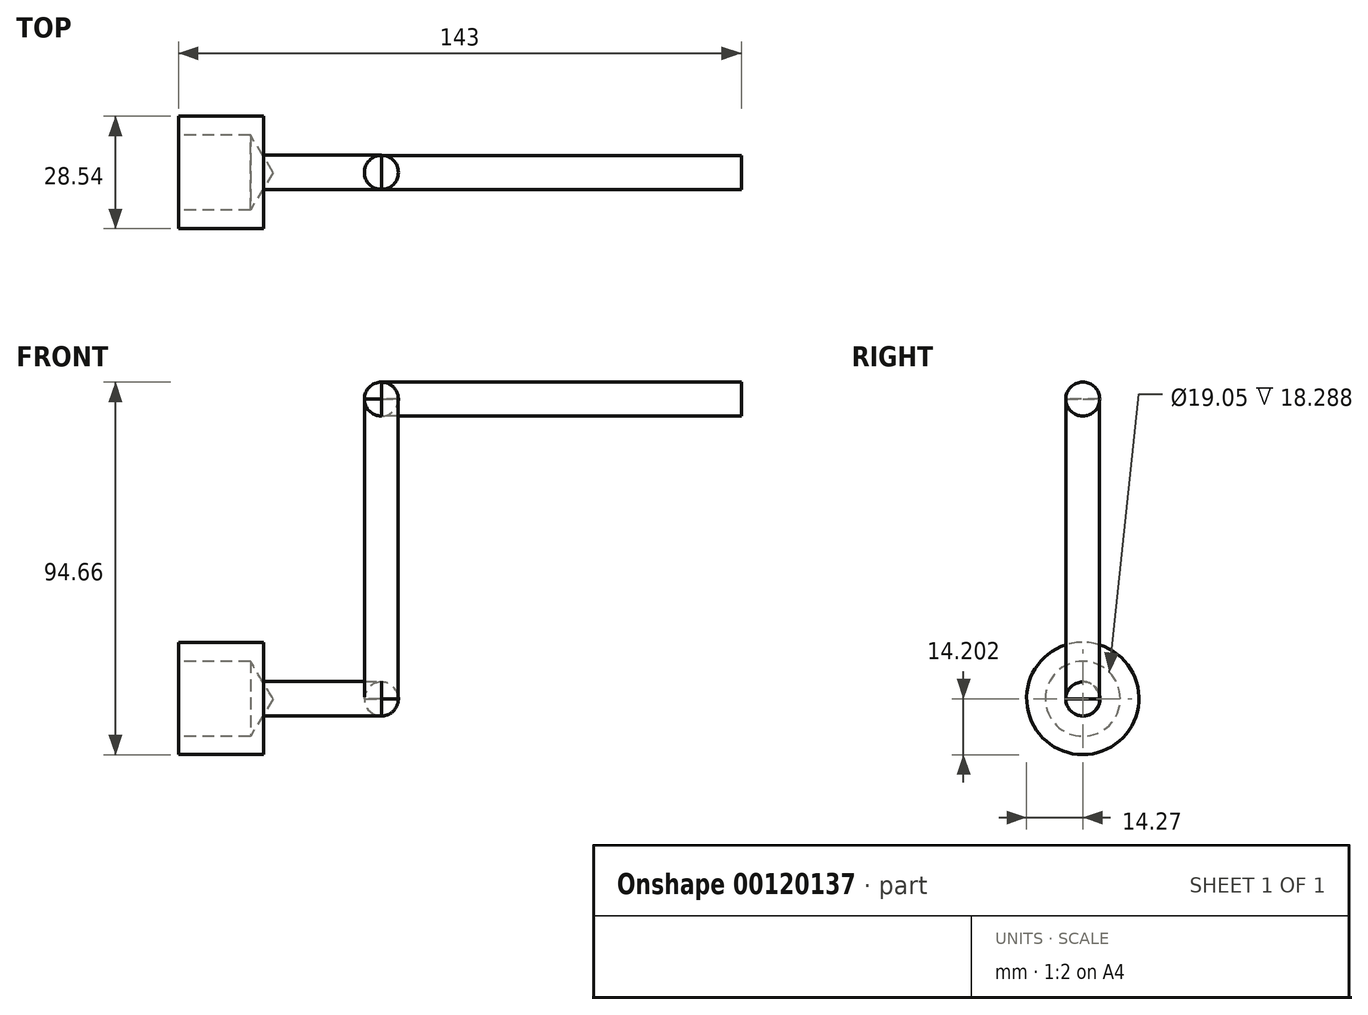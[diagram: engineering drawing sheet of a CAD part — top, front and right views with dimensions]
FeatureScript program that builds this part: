
annotation { "Feature Type Name" : "Feature", "Feature Type Description" : "" }
export const myFeature = defineFeature(function(context is Context, id is Id, definition is map)
    precondition{}
    {
        {
            var Q0;
            Q0=qCreatedBy(makeId("Right.planeOp"),FACE);
            var sketch = newSketch(context, id + "F0", { "sketchPlane" : qUnion([Q0])});
            skCircle(sketch, "E0", {"center": v(0, 45.27) * mm, "radius": 4.32 * mm});
            skLineSegment(sketch, "E1", {"start": v(0, 40.95) * mm, "end": v(0, 49.59) * mm});
            skSolve(sketch);
        }
        {
            var Q0;
            Q0=qCreatedBy(makeId("Right.planeOp"),FACE);
            cPlane(context, id + "F1", {"entities" : qUnion([Q0]), "cplaneType" : CPlaneType.OFFSET, "offset" : 91.44 * mm, "width" : 152.4 * mm, "height" : 152.4 * mm});
        }
        {
            var Q0;
            Q0=qCreatedBy(id+"F1.planeOp",FACE);
            var sketch = newSketch(context, id + "F2", { "sketchPlane" : qUnion([Q0])});
            skCircle(sketch, "E2", {"center": v(0.04, 45.27) * mm, "radius": 3.16 * mm});
            skPoint(sketch, "E2.first.point", {"position": v(0, 48.43) * mm});
            skPoint(sketch, "E2.second.point", {"position": v(0, 42.11) * mm});
            skPoint(sketch, "E2.third.point", {"position": v(3.16, 45.8) * mm});
            skSolve(sketch);
        }
        {
            var Q0;
            {var subQ0=sQuery(id+"F0.wireOp",EDGE,"E1");Q0=makeQuery(id+"F0.imprint","IMPRINT",FACE,{"disambiguationData":[TD([[makeQuery(id+"F0.imprint","IMPRINT",EDGE,{"derivedFrom":subQ0}),-1.0]])]});}
            var Q1;
            {var subQ0=sQuery(id+"F0.wireOp",EDGE,"E1");Q1=makeQuery(id+"F0.imprint","IMPRINT",FACE,{"disambiguationData":[TD([[makeQuery(id+"F0.imprint","IMPRINT",EDGE,{"derivedFrom":subQ0}),1.0]])]});}
            var Q2;
            Q2=sQuery(id+"F0.wireOp",EDGE,"E0");
            extrude(context, id + "F3", {"entities" : qUnion([Q0, Q1]), "surfaceEntities" : qUnion([Q2]), "depth" : 91.44 * mm});
        }
        {
            var Q0;
            {var subQ0=sQuery(id+"F0.wireOp",EDGE,"E1");Q0=makeQuery(id+"F0.imprint","IMPRINT",FACE,{"disambiguationData":[TD([[makeQuery(id+"F0.imprint","IMPRINT",EDGE,{"derivedFrom":subQ0}),1.0]])]});}
            var Q1;
            Q1=sQuery(id+"F0.wireOp",EDGE,"E1");
            revolve(context, id + "F4", {"entities" : qUnion([Q0]), "axis" : qUnion([Q1]), "revolveType" : RevolveType.FULL});
        }
        {
            var Q0;
            Q0=qCreatedBy(makeId("Top.planeOp"),FACE);
            cPlane(context, id + "F5", {"entities" : qUnion([Q0]), "cplaneType" : CPlaneType.OFFSET, "offset" : 45.27 * mm, "width" : 152.4 * mm, "height" : 152.4 * mm});
        }
        {
            var Q0;
            Q0=qCreatedBy(id+"F5.planeOp",FACE);
            var sketch = newSketch(context, id + "F6", { "sketchPlane" : qUnion([Q0])});
            skCircle(sketch, "E3", {"center": v(0, 0) * mm, "radius": 4.29 * mm});
            skSolve(sketch);
        }
        {
            var Q0;
            Q0=qSketchRegion(id+"F6",true);
            extrude(context, id + "F7", {"entities" : qUnion([Q0]), "oppositeDirection" : true, "depth" : 76.2 * mm});
        }
        {
            var Q0;
            Q0=makeQuery(id+"F4.opRevolve","SWEPT_BODY",BODY,{"disambiguationData":[OSD([sQuery(id+"F0.wireOp",EDGE,"E0"),sQuery(id+"F0.wireOp",EDGE,"E1")])]});
            transform(context, id + "F8", {"entities" : qUnion([Q0]), "transformType" : TransformType.TRANSLATION_3D, "dx" : 0 * mm, "dy" : 0 * mm, "dz" : -76.2 * mm, "makeCopy" : true});
        }
        {
            var Q0;
            Q0=qCreatedBy(makeId("Right.planeOp"),FACE);
            var sketch = newSketch(context, id + "F9", { "sketchPlane" : qUnion([Q0])});
            skCircle(sketch, "E4", {"center": v(0, -30.9) * mm, "radius": 4.37 * mm});
            skPoint(sketch, "E4.first.point", {"position": v(0, -35.26) * mm});
            skPoint(sketch, "E4.second.point", {"position": v(-3.92, -32.8) * mm});
            skPoint(sketch, "E4.third.point", {"position": v(3.7, -33.22) * mm});
            skSolve(sketch);
        }
        {
            var Q0;
            Q0=qCreatedBy(makeId("Right.planeOp"),FACE);
            cPlane(context, id + "F10", {"entities" : qUnion([Q0]), "cplaneType" : CPlaneType.OFFSET, "offset" : 51.56 * mm, "oppositeDirection" : true, "width" : 152.4 * mm, "height" : 152.4 * mm});
        }
        {
            var Q0;
            Q0=qCreatedBy(id+"F10.planeOp",FACE);
            var sketch = newSketch(context, id + "F11", { "sketchPlane" : qUnion([Q0])});
            skCircle(sketch, "E5", {"center": v(0, -30.87) * mm, "radius": 14.27 * mm});
            skSolve(sketch);
        }
        {
            var Q0;
            Q0=qCreatedBy(id+"F10.planeOp",FACE);
            cPlane(context, id + "F12", {"entities" : qUnion([Q0]), "cplaneType" : CPlaneType.OFFSET, "offset" : 21.59 * mm, "width" : 152.4 * mm, "height" : 152.4 * mm});
        }
        {
            var Q0;
            Q0=qCreatedBy(id+"F12.planeOp",FACE);
            var sketch = newSketch(context, id + "F13", { "sketchPlane" : qUnion([Q0])});
            skCircle(sketch, "E6", {"center": v(0, -30.8) * mm, "radius": 14.27 * mm});
            skSolve(sketch);
        }
        {
            var Q0;
            Q0=qSketchRegion(id+"F9",true);
            var Q1;
            Q1=sQuery(id+"F9.wireOp",EDGE,"E4");
            extrude(context, id + "F14", {"entities" : qUnion([Q0]), "surfaceEntities" : qUnion([Q1]), "oppositeDirection" : true, "depth" : 29.97 * mm});
        }
        {
            var Q0;
            Q0=makeQuery(id+"F13.imprint","IMPRINT",FACE,{"disambiguationData":[TD([[makeQuery(id+"F13.imprint","IMPRINT",EDGE,{"derivedFrom":sQuery(id+"F13.wireOp",EDGE,"E6")}),1.0]])]});
            extrude(context, id + "F15", {"entities" : qUnion([Q0]), "operationType" : NewBodyOperationType.ADD, "oppositeDirection" : true, "depth" : 21.59 * mm});
        }
        {
            var Q0;
            Q0=sQuery(id+"F11.wireOp",VERTEX,"E5.center");
            var Q1;
            Q1=makeQuery(id+"F14.opExtrude","SWEPT_BODY",BODY,{"disambiguationData":[OSD([sQuery(id+"F9.wireOp",EDGE,"E4")])]});
            hole(context, id + "F16", {"style" : HoleStyle.SIMPLE, "endStyle" : HoleEndStyle.BLIND, "oppositeDirection" : true, "holeDiameter" : 19.05 * mm, "holeDepth" : 18.29 * mm, "startFromSketch" : true, "locations" : qUnion([Q0]), "scope" : qUnion([Q1])});
        }
    });
